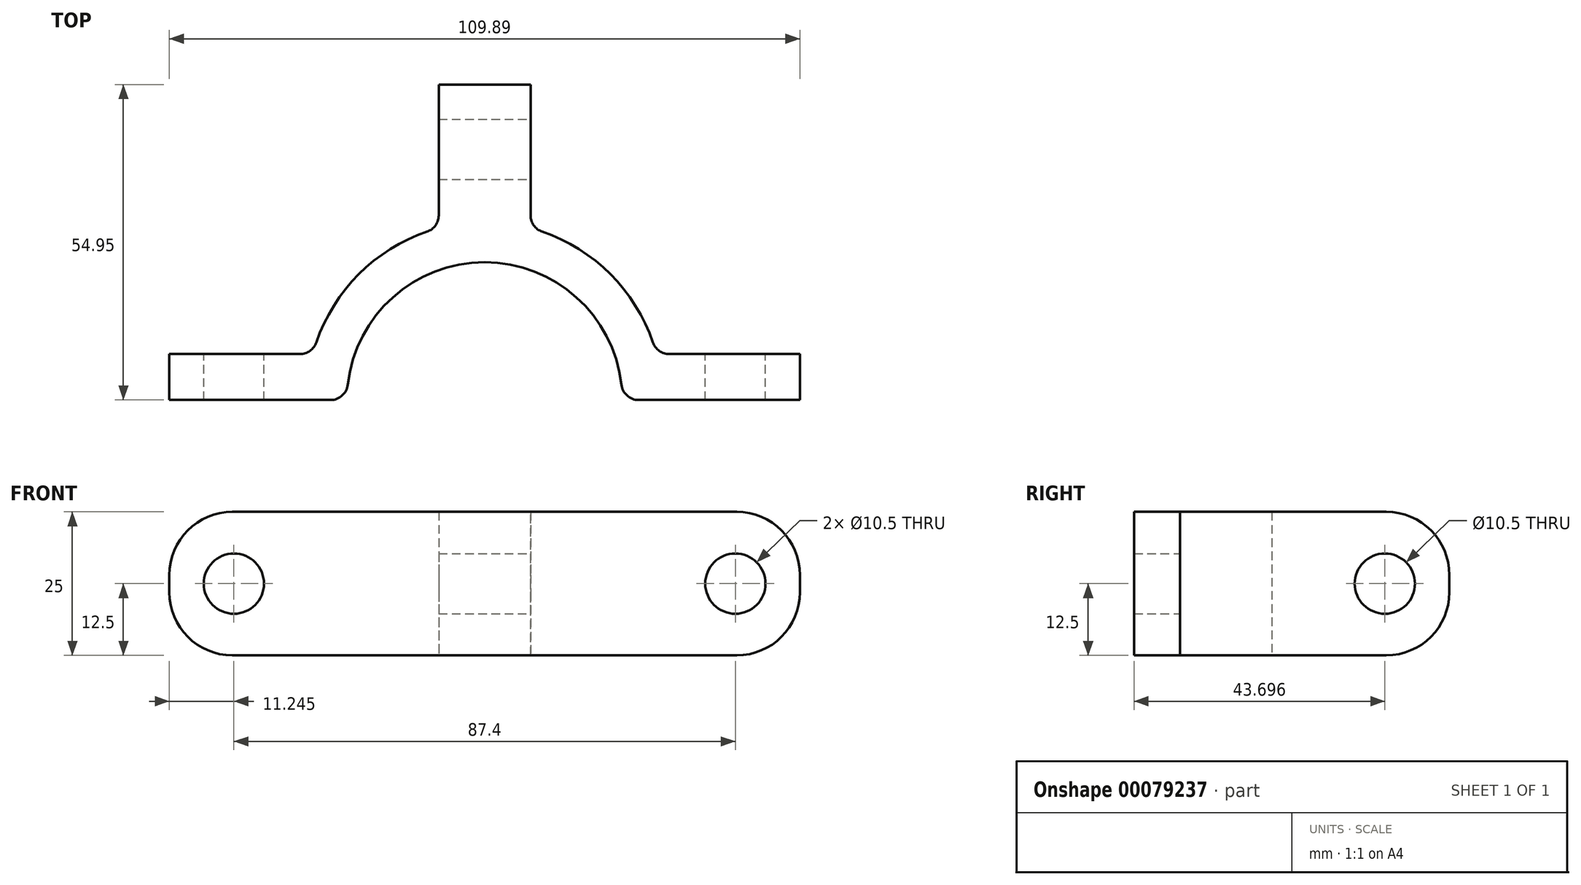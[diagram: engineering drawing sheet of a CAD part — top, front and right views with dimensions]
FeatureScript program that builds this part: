
annotation { "Feature Type Name" : "Feature", "Feature Type Description" : "" }
export const myFeature = defineFeature(function(context is Context, id is Id, definition is map)
    precondition{}
    {
        {
            var Q0;
            Q0=qCreatedBy(makeId("Top.planeOp"),FACE);
            var sketch = newSketch(context, id + "F0", { "sketchPlane" : qUnion([Q0])});
            skLineSegment(sketch, "E0.bottom", {"start": v(-11.48, 44.08) * mm, "end": v(-11.48, 44.08) * mm});
            skLineSegment(sketch, "E0.left", {"start": v(-42.48, 13.08) * mm, "end": v(-42.48, 13.08) * mm});
            skLineSegment(sketch, "E0.right", {"start": v(19.52, 13.08) * mm, "end": v(19.52, 13.08) * mm});
            skPoint(sketch, "E1.visualSharp", {"position": v(-42.48, 44.08) * mm});
            skArc(sketch, "E1.filletArc", {"start": v(-11.48, 44.08) * mm, "mid": v(-33.4, 35) * mm, "end": v(-42.48, 13.08) * mm});
            skPoint(sketch, "E2.visualSharp", {"position": v(19.52, 44.08) * mm});
            skArc(sketch, "E2.filletArc", {"start": v(19.52, 13.08) * mm, "mid": v(10.45, 35) * mm, "end": v(-11.48, 44.08) * mm});
            skPoint(sketch, "E3", {"position": v(-41.42, 21.08) * mm});
            skPoint(sketch, "E4", {"position": v(18.47, 21.08) * mm});
            skLineSegment(sketch, "E5", {"start": v(-41.42, 21.08) * mm, "end": v(-66.42, 21.08) * mm});
            skLineSegment(sketch, "E6", {"start": v(-66.42, 21.08) * mm, "end": v(-66.42, 13.08) * mm});
            skLineSegment(sketch, "E7", {"start": v(-66.42, 13.08) * mm, "end": v(-42.48, 13.08) * mm});
            skLineSegment(sketch, "E8", {"start": v(19.52, 13.08) * mm, "end": v(43.47, 13.08) * mm});
            skLineSegment(sketch, "E9", {"start": v(43.47, 13.08) * mm, "end": v(43.47, 21.08) * mm});
            skLineSegment(sketch, "E10", {"start": v(43.47, 21.08) * mm, "end": v(18.47, 21.08) * mm});
            skLineSegment(sketch, "E11.bottom", {"start": v(-11.48, 37.08) * mm, "end": v(-11.48, 37.08) * mm});
            skLineSegment(sketch, "E11.left", {"start": v(-35.48, 13.08) * mm, "end": v(-35.48, 13.08) * mm});
            skLineSegment(sketch, "E11.right", {"start": v(12.52, 13.08) * mm, "end": v(12.52, 13.08) * mm});
            skPoint(sketch, "E12.visualSharp", {"position": v(12.52, 37.08) * mm});
            skArc(sketch, "E12.filletArc", {"start": v(12.52, 13.08) * mm, "mid": v(5.5, 30.05) * mm, "end": v(-11.48, 37.08) * mm});
            skPoint(sketch, "E13.visualSharp", {"position": v(-35.48, 37.08) * mm});
            skArc(sketch, "E13.filletArc", {"start": v(-11.48, 37.08) * mm, "mid": v(-28.45, 30.05) * mm, "end": v(-35.48, 13.08) * mm});
            skLineSegment(sketch, "E14", {"start": v(-35.48, 13.08) * mm, "end": v(-42.48, 13.08) * mm});
            skLineSegment(sketch, "E15", {"start": v(12.52, 13.08) * mm, "end": v(19.52, 13.08) * mm});
            skLineSegment(sketch, "E16", {"start": v(-19.48, 43.03) * mm, "end": v(-19.48, 68.03) * mm});
            skLineSegment(sketch, "E17", {"start": v(-3.48, 43.03) * mm, "end": v(-3.48, 68.03) * mm});
            skLineSegment(sketch, "E18", {"start": v(-3.48, 68.03) * mm, "end": v(-19.48, 68.03) * mm});
            skSolve(sketch);
        }
        {
            var Q0;
            {var subQ2=sQuery(id+"F0.wireOp",EDGE,"E5");Q0=makeQuery(id+"F0.imprint","IMPRINT",FACE,{"disambiguationData":[TD([[makeQuery(id+"F0.imprint","IMPRINT",EDGE,{"derivedFrom":subQ2}),1.0]])]});}
            var Q1;
            {var subQ0=sQuery(id+"F0.wireOp",EDGE,"E8");Q1=makeQuery(id+"F0.imprint","IMPRINT",FACE,{"disambiguationData":[TD([[makeQuery(id+"F0.imprint","IMPRINT",EDGE,{"derivedFrom":subQ0}),1.0]])]});}
            var Q2;
            Q2=makeQuery(id+"F0.imprint","IMPRINT",FACE,{"disambiguationData":[TD([[makeQuery(id+"F0.imprint","IMPRINT",EDGE,{"derivedFrom":sQuery(id+"F0.wireOp",EDGE,"E12.filletArc")}),-1.0]])]});
            var Q3;
            {var subQ4=sQuery(id+"F0.wireOp",EDGE,"E16");Q3=makeQuery(id+"F0.imprint","IMPRINT",FACE,{"disambiguationData":[TD([[makeQuery(id+"F0.imprint","IMPRINT",EDGE,{"derivedFrom":subQ4}),-1.0]])]});}
            extrude(context, id + "F1", {"entities" : qUnion([Q0, Q1, Q2, Q3]), "depth" : 25 * mm});
        }
        {
            var Q0;
            Q0=makeQuery(id+"F1.opExtrude","CAP_EDGE",EDGE,{"disambiguationData":[OSD([sQuery(id+"F0.wireOp",EDGE,"E9")])],"isStart":true});
            var Q1;
            Q1=makeQuery(id+"F1.opExtrude","CAP_EDGE",EDGE,{"disambiguationData":[OSD([sQuery(id+"F0.wireOp",EDGE,"E9")])],"isStart":false});
            var Q2;
            Q2=makeQuery(id+"F1.opExtrude","CAP_EDGE",EDGE,{"disambiguationData":[OSD([sQuery(id+"F0.wireOp",EDGE,"E6")])],"isStart":false});
            var Q3;
            Q3=makeQuery(id+"F1.opExtrude","CAP_EDGE",EDGE,{"disambiguationData":[OSD([sQuery(id+"F0.wireOp",EDGE,"E6")])],"isStart":true});
            var Q4;
            Q4=makeQuery(id+"F1.opExtrude","CAP_EDGE",EDGE,{"disambiguationData":[OSD([sQuery(id+"F0.wireOp",EDGE,"E18")])],"isStart":true});
            var Q5;
            Q5=makeQuery(id+"F1.opExtrude","CAP_EDGE",EDGE,{"disambiguationData":[OSD([sQuery(id+"F0.wireOp",EDGE,"E18")])],"isStart":false});
            fillet(context, id + "F2", {"entities" : qUnion([Q0, Q1, Q2, Q3, Q4, Q5]), "radius" : 11 * mm, "tangentPropagation" : true, "allowEdgeOverflow" : false});
        }
        {
            var Q0;
            Q0=makeQuery(id+"F1.opExtrude","SWEPT_EDGE",EDGE,{"disambiguationData":[OSD([sQuery(id+"F0.wireOp",EDGE,"E13.filletArc"),sQuery(id+"F0.wireOp",EDGE,"E14")])]});
            var Q1;
            Q1=makeQuery(id+"F1.opExtrude","SWEPT_EDGE",EDGE,{"disambiguationData":[OSD([sQuery(id+"F0.wireOp",EDGE,"E12.filletArc"),sQuery(id+"F0.wireOp",EDGE,"E15")])]});
            fillet(context, id + "F3", {"entities" : qUnion([Q0, Q1]), "radius" : 3 * mm, "tangentPropagation" : true, "allowEdgeOverflow" : false});
        }
        {
            var Q0;
            Q0=makeQuery(id+"F1.opExtrude","SWEPT_EDGE",EDGE,{"disambiguationData":[OSD([sQuery(id+"F0.wireOp",EDGE,"E1.filletArc"),sQuery(id+"F0.wireOp",EDGE,"E5")])]});
            var Q1;
            Q1=makeQuery(id+"F1.opExtrude","SWEPT_EDGE",EDGE,{"disambiguationData":[OSD([sQuery(id+"F0.wireOp",EDGE,"E2.filletArc"),sQuery(id+"F0.wireOp",EDGE,"E10")])]});
            var Q2;
            Q2=makeQuery(id+"F1.opExtrude","SWEPT_EDGE",EDGE,{"disambiguationData":[OSD([sQuery(id+"F0.wireOp",EDGE,"E2.filletArc"),sQuery(id+"F0.wireOp",EDGE,"E17")])]});
            var Q3;
            Q3=makeQuery(id+"F1.opExtrude","SWEPT_EDGE",EDGE,{"disambiguationData":[OSD([sQuery(id+"F0.wireOp",EDGE,"E1.filletArc"),sQuery(id+"F0.wireOp",EDGE,"E16")])]});
            fillet(context, id + "F4", {"entities" : qUnion([Q0, Q1, Q2, Q3]), "radius" : 3 * mm, "tangentPropagation" : true, "allowEdgeOverflow" : false});
        }
        {
            var Q0;
            Q0=makeQuery(id+"F1.opExtrude","SWEPT_FACE",FACE,{"disambiguationData":[OSD([sQuery(id+"F0.wireOp",EDGE,"E5")])]});
            var sketch = newSketch(context, id + "F5", { "sketchPlane" : qUnion([Q0])});
            skPoint(sketch, "E19", {"position": v(55.17, 12.5) * mm});
            skPoint(sketch, "E20", {"position": v(-32.22, 12.5) * mm});
            skSolve(sketch);
        }
        {
            var Q0;
            Q0=sQuery(id+"F5.wireOp",VERTEX,"E19");
            var Q1;
            Q1=sQuery(id+"F5.wireOp",VERTEX,"E20");
            var Q2;
            Q2=makeQuery(id+"F1.opExtrude","SWEPT_BODY",BODY,{"disambiguationData":[OSD([sQuery(id+"F0.wireOp",EDGE,"E1.filletArc"),sQuery(id+"F0.wireOp",EDGE,"E2.filletArc"),sQuery(id+"F0.wireOp",EDGE,"E5"),sQuery(id+"F0.wireOp",EDGE,"E6"),sQuery(id+"F0.wireOp",EDGE,"E7"),sQuery(id+"F0.wireOp",EDGE,"E8"),sQuery(id+"F0.wireOp",EDGE,"E9"),sQuery(id+"F0.wireOp",EDGE,"E10"),sQuery(id+"F0.wireOp",EDGE,"E12.filletArc"),sQuery(id+"F0.wireOp",EDGE,"E13.filletArc"),sQuery(id+"F0.wireOp",EDGE,"E14"),sQuery(id+"F0.wireOp",EDGE,"E15")])]});
            hole(context, id + "F6", {"style" : HoleStyle.SIMPLE, "endStyle" : HoleEndStyle.THROUGH, "holeDiameter" : 10.5 * mm, "locations" : qUnion([Q0, Q1]), "scope" : qUnion([Q2]), "isTappedThrough" : true});
        }
        {
            var Q0;
            Q0=makeQuery(id+"F1.opExtrude","SWEPT_FACE",FACE,{"disambiguationData":[OSD([sQuery(id+"F0.wireOp",EDGE,"E17")])]});
            var sketch = newSketch(context, id + "F7", { "sketchPlane" : qUnion([Q0])});
            skPoint(sketch, "E21", {"position": v(56.78, 12.5) * mm});
            skSolve(sketch);
        }
        {
            var Q0;
            Q0=sQuery(id+"F7.wireOp",VERTEX,"E21");
            var Q1;
            Q1=makeQuery(id+"F1.opExtrude","SWEPT_BODY",BODY,{"disambiguationData":[OSD([sQuery(id+"F0.wireOp",EDGE,"E1.filletArc"),sQuery(id+"F0.wireOp",EDGE,"E2.filletArc"),sQuery(id+"F0.wireOp",EDGE,"E5"),sQuery(id+"F0.wireOp",EDGE,"E6"),sQuery(id+"F0.wireOp",EDGE,"E7"),sQuery(id+"F0.wireOp",EDGE,"E8"),sQuery(id+"F0.wireOp",EDGE,"E9"),sQuery(id+"F0.wireOp",EDGE,"E10"),sQuery(id+"F0.wireOp",EDGE,"E12.filletArc"),sQuery(id+"F0.wireOp",EDGE,"E13.filletArc"),sQuery(id+"F0.wireOp",EDGE,"E14"),sQuery(id+"F0.wireOp",EDGE,"E15"),sQuery(id+"F0.wireOp",EDGE,"E16"),sQuery(id+"F0.wireOp",EDGE,"E17"),sQuery(id+"F0.wireOp",EDGE,"E18")])]});
            hole(context, id + "F8", {"style" : HoleStyle.SIMPLE, "endStyle" : HoleEndStyle.THROUGH, "holeDiameter" : 10.5 * mm, "locations" : qUnion([Q0]), "scope" : qUnion([Q1]), "isTappedThrough" : true});
        }
    });
